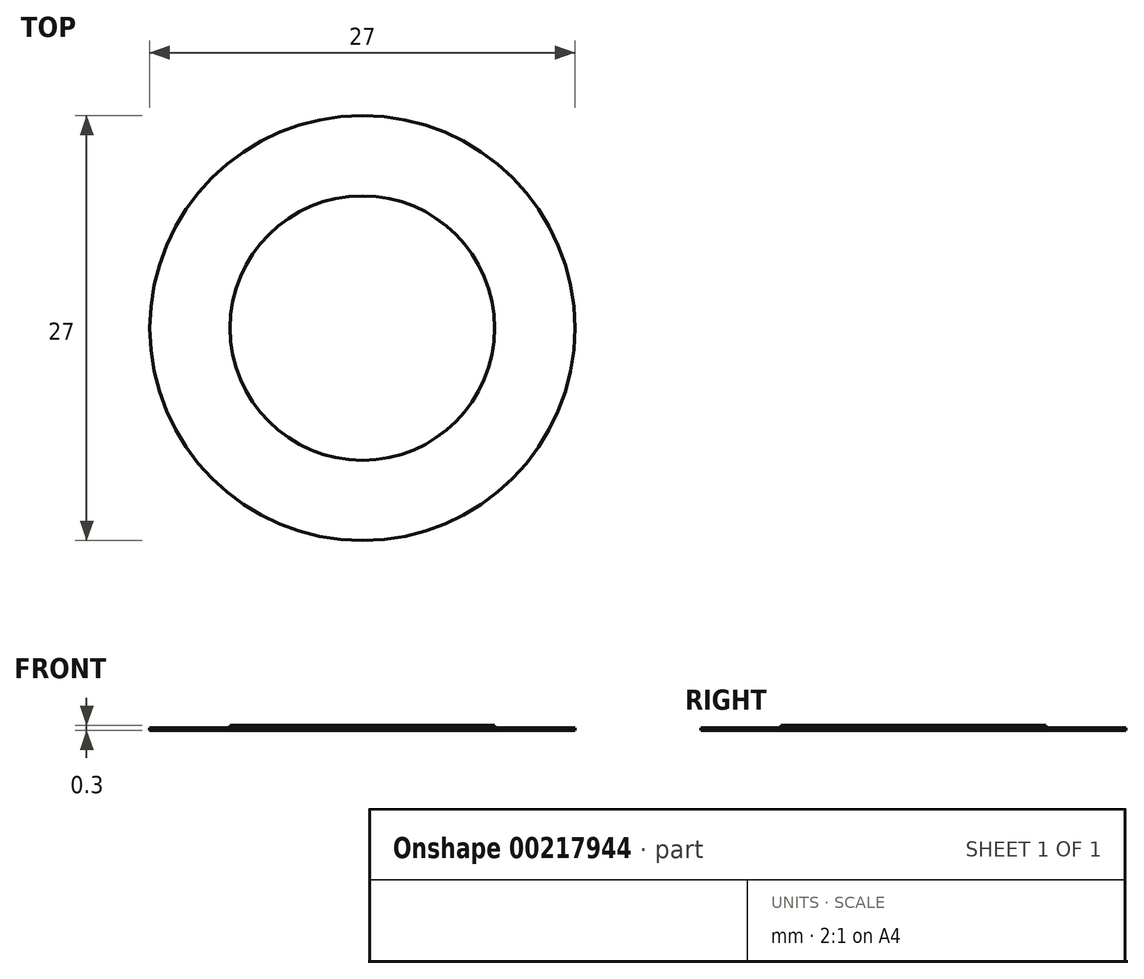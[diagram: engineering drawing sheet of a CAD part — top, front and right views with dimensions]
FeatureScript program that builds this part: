
annotation { "Feature Type Name" : "Feature", "Feature Type Description" : "" }
export const myFeature = defineFeature(function(context is Context, id is Id, definition is map)
    precondition{}
    {
        {
            var Q0;
            Q0=qCreatedBy(makeId("Top.planeOp"),FACE);
            var sketch = newSketch(context, id + "F0", { "sketchPlane" : qUnion([Q0])});
            skCircle(sketch, "E0", {"center": v(0, 0) * mm, "radius": 13.5 * mm});
            skCircle(sketch, "E1", {"center": v(0, 0) * mm, "radius": 8.4 * mm});
            skSolve(sketch);
        }
        {
            var Q0;
            Q0 = qSketchRegion(id + "F0", true);
            extrude(context, id + "F1", {"entities" : qUnion([Q0]), "depth" : 0.16 * mm});
        }
        {
            var Q0;
            Q0=makeQuery(id+"F0.imprint","IMPRINT",FACE,{"disambiguationData":[TD([[makeQuery(id+"F0.imprint","IMPRINT",EDGE,{"derivedFrom":sQuery(id+"F0.wireOp",EDGE,"E1")}),1.0]])]});
            extrude(context, id + "F2", {"entities" : qUnion([Q0]), "operationType" : NewBodyOperationType.ADD, "depth" : 0.3 * mm});
        }
    });
